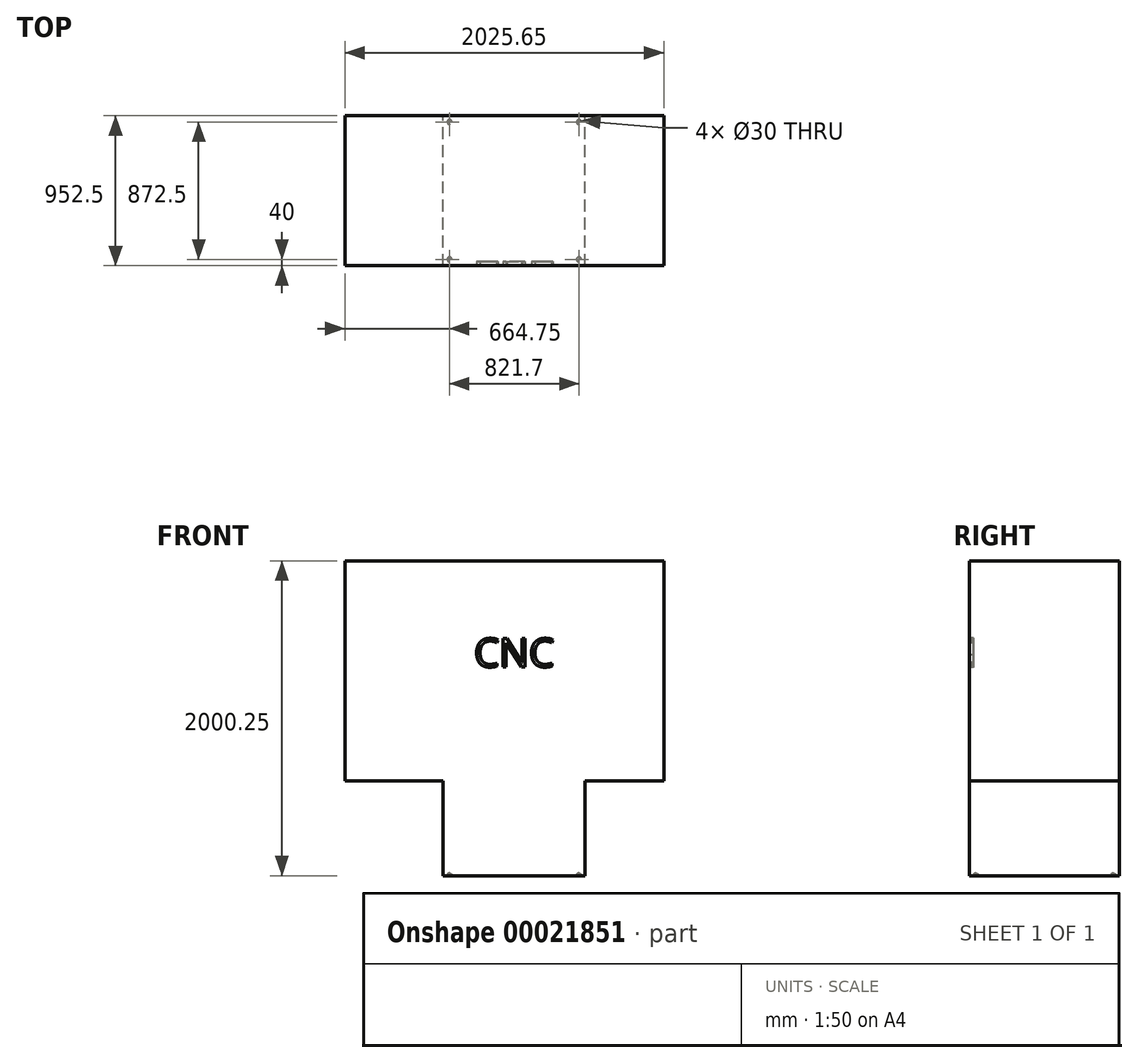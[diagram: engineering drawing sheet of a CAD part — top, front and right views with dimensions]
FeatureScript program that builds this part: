
annotation { "Feature Type Name" : "Feature", "Feature Type Description" : "" }
export const myFeature = defineFeature(function(context is Context, id is Id, definition is map)
    precondition{}
    {
        {
            var Q0;
            Q0=qCreatedBy(makeId("Top.planeOp"),FACE);
            var sketch = newSketch(context, id + "F0", { "sketchPlane" : qUnion([Q0])});
            skLineSegment(sketch, "E0.bottom", {"start": v(0, 0) * mm, "end": v(901.7, 0) * mm});
            skLineSegment(sketch, "E0.top", {"start": v(0, 952.5) * mm, "end": v(901.7, 952.5) * mm});
            skLineSegment(sketch, "E0.left", {"start": v(0, 0) * mm, "end": v(0, 952.5) * mm});
            skLineSegment(sketch, "E0.right", {"start": v(901.7, 0) * mm, "end": v(901.7, 952.5) * mm});
            skSolve(sketch);
        }
        {
            var Q0;
            Q0 = qSketchRegion(id + "F0", true);
            extrude(context, id + "F1", {"entities" : qUnion([Q0]), "depth" : (23.75 * 25.4) * mm});
        }
        {
            var Q0;
            Q0=makeQuery(id+"F1.opExtrude","CAP_FACE",FACE,{"disambiguationData":[OSD([sQuery(id+"F0.wireOp",EDGE,"E0.bottom"),sQuery(id+"F0.wireOp",EDGE,"E0.top"),sQuery(id+"F0.wireOp",EDGE,"E0.left"),sQuery(id+"F0.wireOp",EDGE,"E0.right")])],"isStart":true});
            var sketch = newSketch(context, id + "F2", { "sketchPlane" : qUnion([Q0])});
            skPoint(sketch, "E1", {"position": v(40, -40) * mm});
            skPoint(sketch, "E2", {"position": v(861.7, -40) * mm});
            skPoint(sketch, "E3", {"position": v(861.7, -912.5) * mm});
            skPoint(sketch, "E4", {"position": v(40, -912.5) * mm});
            skSolve(sketch);
        }
        {
            var Q0;
            Q0=sQuery(id+"F2.wireOp",VERTEX,"E4");
            var Q1;
            Q1=sQuery(id+"F2.wireOp",VERTEX,"E1");
            var Q2;
            Q2=sQuery(id+"F2.wireOp",VERTEX,"E2");
            var Q3;
            Q3=sQuery(id+"F2.wireOp",VERTEX,"E3");
            var Q4;
            Q4=makeQuery(id+"F1.opExtrude","SWEPT_BODY",BODY,{"disambiguationData":[OSD([sQuery(id+"F0.wireOp",EDGE,"E0.bottom"),sQuery(id+"F0.wireOp",EDGE,"E0.top"),sQuery(id+"F0.wireOp",EDGE,"E0.left"),sQuery(id+"F0.wireOp",EDGE,"E0.right")])]});
            hole(context, id + "F3", {"style" : HoleStyle.SIMPLE, "holeDiameter" : 30 * mm, "endStyle" : HoleEndStyle.BLIND, "holeDepth" : 10 * mm, "locations" : qUnion([Q0, Q1, Q2, Q3]), "scope" : qUnion([Q4])});
        }
        {
            var Q0;
            Q0=makeQuery(id+"F1.opExtrude","CAP_FACE",FACE,{"disambiguationData":[OSD([sQuery(id+"F0.wireOp",EDGE,"E0.bottom"),sQuery(id+"F0.wireOp",EDGE,"E0.top"),sQuery(id+"F0.wireOp",EDGE,"E0.left"),sQuery(id+"F0.wireOp",EDGE,"E0.right")])],"isStart":false});
            var sketch = newSketch(context, id + "F4", { "sketchPlane" : qUnion([Q0])});
            skLineSegment(sketch, "E5.bottom", {"start": v(-624.75, 952.5) * mm, "end": v(1400.9, 952.5) * mm});
            skLineSegment(sketch, "E5.top", {"start": v(-624.75, 0) * mm, "end": v(1400.9, 0) * mm});
            skLineSegment(sketch, "E5.left", {"start": v(-624.75, 952.5) * mm, "end": v(-624.75, 0) * mm});
            skLineSegment(sketch, "E5.right", {"start": v(1400.9, 952.5) * mm, "end": v(1400.9, 0) * mm});
            skSolve(sketch);
        }
        {
            var Q0;
            Q0 = qSketchRegion(id + "F4", true);
            extrude(context, id + "F5", {"entities" : qUnion([Q0]), "operationType" : NewBodyOperationType.ADD, "depth" : (55 * 25.4) * mm});
        }
        {
            var Q0;
            Q0=makeQuery(id+"F5.boolean.opBoolean","MERGE",FACE,{"derivedFrom":[makeQuery(id+"F1.opExtrude","SWEPT_FACE",FACE,{"disambiguationData":[OSD([sQuery(id+"F0.wireOp",EDGE,"E0.bottom")])]}),makeQuery(id+"F5.opExtrude","SWEPT_FACE",FACE,{"disambiguationData":[OSD([sQuery(id+"F4.wireOp",EDGE,"E5.top")])]})]});
            var sketch = newSketch(context, id + "F6", { "sketchPlane" : qUnion([Q0])});
            skText(sketch, "E6", { "text": "CNC\n", "fontName": "OpenSans-Regular.ttf"});
            const initialGuessF6  = {"E6": [0.19616, 1.32699, 1, 0, 0.18127]};
            skSetInitialGuess(sketch, initialGuessF6);
            skSolve(sketch);
        }
        {
            var Q0;
            Q0 = qSketchRegion(id + "F6", true);
            extrude(context, id + "F7", {"entities" : qUnion([Q0]), "operationType" : NewBodyOperationType.REMOVE, "oppositeDirection" : true, "depth" : 25 * mm});
        }
    });
